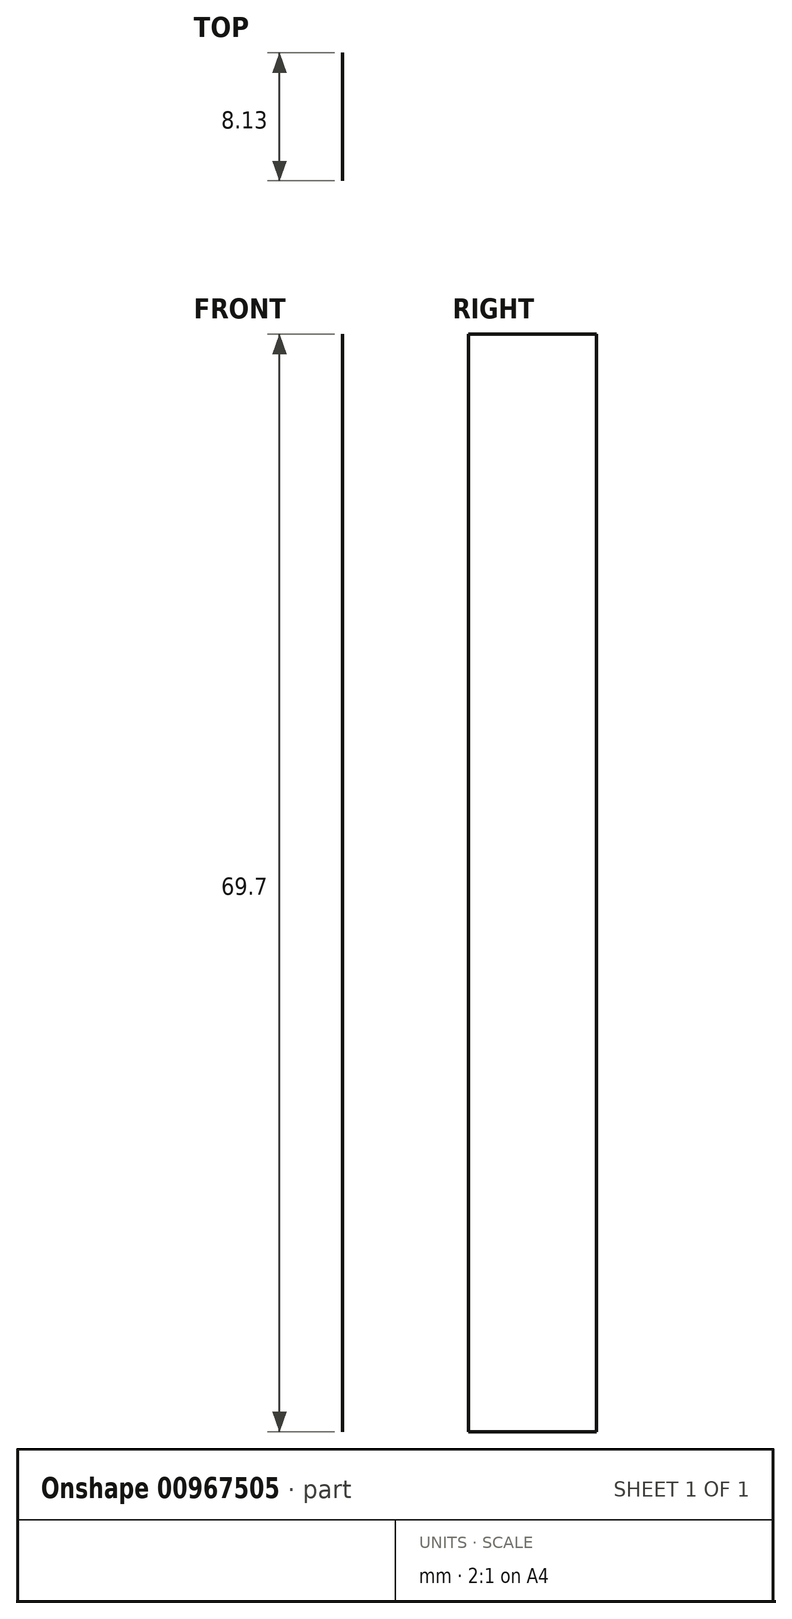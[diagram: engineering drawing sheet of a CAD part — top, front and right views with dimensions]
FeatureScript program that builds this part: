
annotation { "Feature Type Name" : "Feature", "Feature Type Description" : "" }
export const myFeature = defineFeature(function(context is Context, id is Id, definition is map)
    precondition{}
    {
        {
            var Q0;
            Q0=qCreatedBy(makeId("Front.planeOp"),FACE);
            var sketch = newSketch(context, id + "F0", { "sketchPlane" : qUnion([Q0])});
            skLineSegment(sketch, "E0", {"start": v(0, 19.57) * mm, "end": v(0, -43.87) * mm});
            skLineSegment(sketch, "E1", {"start": v(0, -43.87) * mm, "end": v(48.88, -30.05) * mm});
            skLineSegment(sketch, "E2", {"start": v(48.88, -30.05) * mm, "end": v(48.88, -17.33) * mm});
            skLineSegment(sketch, "E3", {"start": v(48.88, -17.33) * mm, "end": v(56.75, -14.94) * mm});
            skLineSegment(sketch, "E4", {"start": v(56.75, -14.94) * mm, "end": v(56.75, -32.91) * mm});
            skLineSegment(sketch, "E5", {"start": v(56.75, -32.91) * mm, "end": v(0, -49.3) * mm});
            skLineSegment(sketch, "E6", {"start": v(0, -49.3) * mm, "end": v(-6.98, -51.42) * mm});
            skLineSegment(sketch, "E7", {"start": v(-6.98, -51.42) * mm, "end": v(-6.98, 17.52) * mm});
            skLineSegment(sketch, "E8", {"start": v(-6.98, 17.52) * mm, "end": v(0, 19.57) * mm});
            skLineSegment(sketch, "E9", {"start": v(-20.96, 14.5) * mm, "end": v(-20.96, -55.2) * mm});
            skLineSegment(sketch, "E10", {"start": v(-20.96, -55.2) * mm, "end": v(-24.26, -55.2) * mm});
            skLineSegment(sketch, "E11", {"start": v(-24.26, -55.2) * mm, "end": v(-24.26, 13.66) * mm});
            skLineSegment(sketch, "E12", {"start": v(-24.26, 13.66) * mm, "end": v(-20.96, 14.5) * mm});
            skSolve(sketch);
        }
        {
            var Q0;
            Q0=sQuery(id+"F0.wireOp",EDGE,"E9");
            extrude(context, id + "F1", {"bodyType" : ToolBodyType.SURFACE, "surfaceEntities" : qUnion([Q0]), "depth" : 8.13 * mm, "offsetDistance" : 25.4 * mm});
        }
    });
